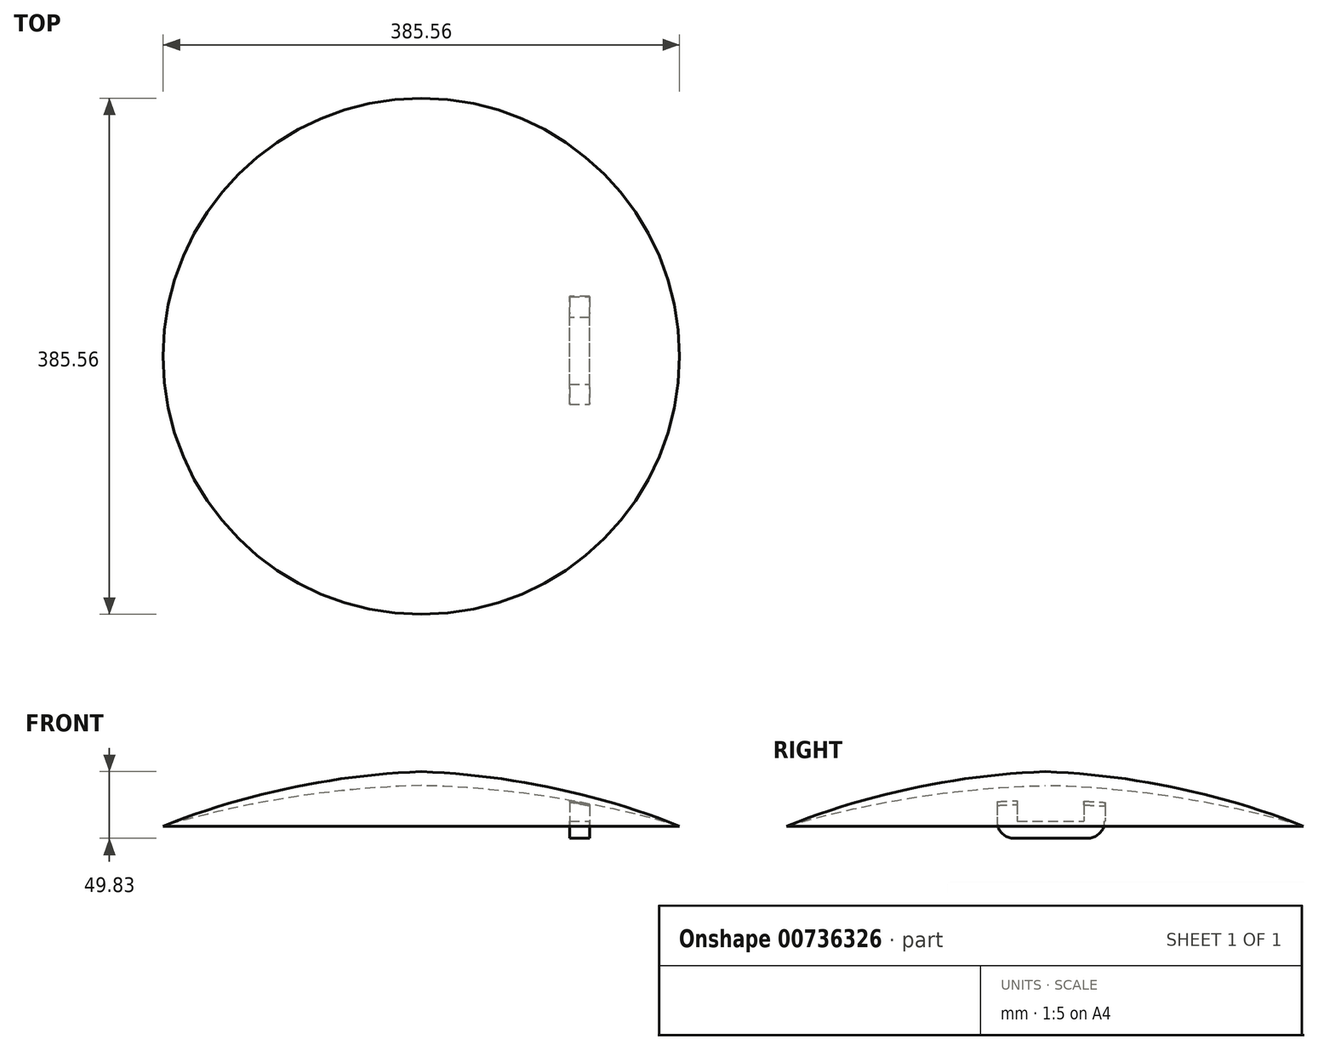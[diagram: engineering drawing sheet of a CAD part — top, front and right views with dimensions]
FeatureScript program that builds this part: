
annotation { "Feature Type Name" : "Feature", "Feature Type Description" : "" }
export const myFeature = defineFeature(function(context is Context, id is Id, definition is map)
    precondition{}
    {
        {
            var Q0;
            Q0=qCreatedBy(makeId("Right.planeOp"),FACE);
            var sketch = newSketch(context, id + "F0", { "sketchPlane" : qUnion([Q0])});
            skArc(sketch, "E0", {"start": v(0, 37.13) * mm, "mid": v(-98.12, 24.97) * mm, "end": v(-192.78, -3.55) * mm});
            skLineSegment(sketch, "E1", {"start": v(0, 37.13) * mm, "end": v(0, 26.73) * mm});
            skArc(sketch, "E2", {"start": v(0, 26.73) * mm, "mid": v(-97.38, 17.92) * mm, "end": v(-192.78, -3.55) * mm});
            skSolve(sketch);
        }
        {
            var Q0;
            Q0=makeQuery(id+"F0.imprint","IMPRINT",FACE,{"disambiguationData":[TD([[makeQuery(id+"F0.imprint","IMPRINT",EDGE,{"derivedFrom":sQuery(id+"F0.wireOp",EDGE,"E0")}),1.0]])]});
            var Q1;
            Q1=sQuery(id+"F0.wireOp",EDGE,"E1");
            revolve(context, id + "F1", {"surfaceOperationType" : NewSurfaceOperationType.NEW, "entities" : qUnion([Q0]), "axis" : qUnion([Q1]), "revolveType" : RevolveType.FULL});
        }
        {
            var Q0;
            Q0=qCreatedBy(makeId("Top.planeOp"),FACE);
            var sketch = newSketch(context, id + "F2", { "sketchPlane" : qUnion([Q0])});
            skLineSegment(sketch, "E3.bottom", {"start": v(110.57, -35.85) * mm, "end": v(125.67, -35.85) * mm});
            skLineSegment(sketch, "E3.top", {"start": v(110.57, -20.76) * mm, "end": v(125.67, -20.76) * mm});
            skLineSegment(sketch, "E3.left", {"start": v(110.57, -35.85) * mm, "end": v(110.57, -20.76) * mm});
            skLineSegment(sketch, "E3.right", {"start": v(125.67, -35.85) * mm, "end": v(125.67, -20.76) * mm});
            skLineSegment(sketch, "E4.bottom", {"start": v(125.67, 29.06) * mm, "end": v(110.57, 29.06) * mm});
            skLineSegment(sketch, "E4.top", {"start": v(125.67, 44.9) * mm, "end": v(110.57, 44.9) * mm});
            skLineSegment(sketch, "E4.left", {"start": v(125.67, 29.06) * mm, "end": v(125.67, 44.9) * mm});
            skLineSegment(sketch, "E4.right", {"start": v(110.57, 29.06) * mm, "end": v(110.57, 44.9) * mm});
            skSolve(sketch);
        }
        {
            var Q0;
            Q0=makeQuery(id+"F2.imprint","IMPRINT",FACE,{"disambiguationData":[TD([[makeQuery(id+"F2.imprint","IMPRINT",EDGE,{"derivedFrom":sQuery(id+"F2.wireOp",EDGE,"E3.bottom")}),1.0]])]});
            var Q1;
            Q1=makeQuery(id+"F2.imprint","IMPRINT",FACE,{"disambiguationData":[TD([[makeQuery(id+"F2.imprint","IMPRINT",EDGE,{"derivedFrom":sQuery(id+"F2.wireOp",EDGE,"E4.bottom")}),-1.0]])]});
            extrude(context, id + "F3", {"entities" : qUnion([Q0, Q1]), "operationType" : NewBodyOperationType.ADD, "endBound" : BoundingType.UP_TO_NEXT, "depth" : 25.4 * mm, "offsetDistance" : 25.4 * mm});
        }
        {
            var Q0;
            Q0=makeQuery(id+"F3.opExtrude","CAP_FACE",FACE,{"disambiguationData":[OSD([sQuery(id+"F2.wireOp",EDGE,"E3.bottom"),sQuery(id+"F2.wireOp",EDGE,"E3.top"),sQuery(id+"F2.wireOp",EDGE,"E3.left"),sQuery(id+"F2.wireOp",EDGE,"E3.right")])],"isStart":true});
            var sketch = newSketch(context, id + "F4", { "sketchPlane" : qUnion([Q0])});
            skLineSegment(sketch, "E5.bottom", {"start": v(110.57, 35.85) * mm, "end": v(125.67, 35.85) * mm});
            skLineSegment(sketch, "E5.top", {"start": v(110.57, -44.4) * mm, "end": v(125.67, -44.4) * mm});
            skLineSegment(sketch, "E5.left", {"start": v(110.57, 35.85) * mm, "end": v(110.57, -44.4) * mm});
            skLineSegment(sketch, "E5.right", {"start": v(125.67, 35.85) * mm, "end": v(125.67, -44.4) * mm});
            skSolve(sketch);
        }
        {
            var Q0;
            {var subQ0=sQuery(id+"F4.wireOp",EDGE,"E5.bottom");Q0=makeQuery(id+"F4.imprint","IMPRINT",FACE,{"disambiguationData":[TD([[makeQuery(id+"F4.imprint","IMPRINT",EDGE,{"derivedFrom":subQ0}),-1.0]])]});}
            var Q1;
            {var subQ0=sQuery(id+"F4.wireOp",EDGE,"E5.top");Q1=makeQuery(id+"F4.imprint","IMPRINT",FACE,{"disambiguationData":[TD([[makeQuery(id+"F4.imprint","IMPRINT",EDGE,{"derivedFrom":subQ0}),1.0]])]});}
            extrude(context, id + "F5", {"entities" : qUnion([Q0, Q1]), "operationType" : NewBodyOperationType.ADD, "depth" : 12.7 * mm, "offsetDistance" : 25.4 * mm});
        }
        {
            var Q0;
            Q0=makeQuery(id+"F5.opExtrude","CAP_EDGE",EDGE,{"disambiguationData":[OSD([sQuery(id+"F4.wireOp",EDGE,"E5.bottom")])],"isStart":false});
            var Q1;
            Q1=makeQuery(id+"F5.opExtrude","CAP_EDGE",EDGE,{"disambiguationData":[OSD([sQuery(id+"F4.wireOp",EDGE,"E5.top")])],"isStart":false});
            fillet(context, id + "F6", {"entities" : qUnion([Q0, Q1]), "radius" : 12.7 * mm, "tangentPropagation" : true, "allowEdgeOverflow" : false});
        }
    });
